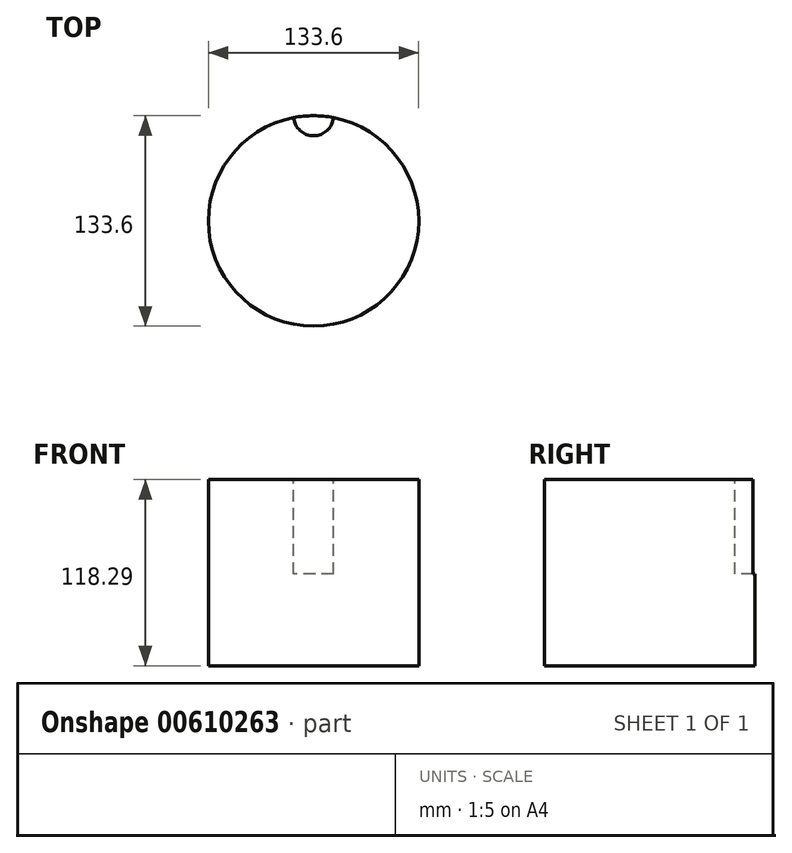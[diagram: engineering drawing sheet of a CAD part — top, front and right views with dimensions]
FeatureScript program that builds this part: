
annotation { "Feature Type Name" : "Feature", "Feature Type Description" : "" }
export const myFeature = defineFeature(function(context is Context, id is Id, definition is map)
    precondition{}
    {
        {
            var Q0;
            Q0=qCreatedBy(makeId("Top.planeOp"),FACE);
            var sketch = newSketch(context, id + "F0", { "sketchPlane" : qUnion([Q0])});
            skCircle(sketch, "E0", {"center": v(0, 0) * mm, "radius": 66.8 * mm});
            skSolve(sketch);
        }
        {
            var Q0;
            Q0 = qSketchRegion(id + "F0", true);
            extrude(context, id + "F1", {"entities" : qUnion([Q0]), "depth" : 118.3 * mm, "offsetDistance" : 25 * mm});
        }
        {
            var Q0;
            Q0=makeQuery(id+"F1.opExtrude","CAP_FACE",FACE,{"disambiguationData":[OSD([sQuery(id+"F0.wireOp",EDGE,"E0")])],"isStart":false});
            var sketch = newSketch(context, id + "F2", { "sketchPlane" : qUnion([Q0])});
            skSolve(sketch);
        }
        {
            var Q0;
            Q0=makeQuery(id+"F2.imprint","IMPRINT",FACE,{"disambiguationData":[TD([[makeQuery(id+"F2.imprint","IMPRINT",EDGE,{"derivedFrom":makeQuery(id+"F1.opExtrude","CAP_EDGE",EDGE,{"disambiguationData":[OSD([sQuery(id+"F0.wireOp",EDGE,"E0")])],"isStart":false})}),1.0]])]});
            var sketch = newSketch(context, id + "F3", { "sketchPlane" : qUnion([Q0])});
            skCircle(sketch, "E1", {"center": v(0, 66.75) * mm, "radius": 12.68 * mm});
            skSolve(sketch);
        }
        {
            var Q0;
            {var subQ0=sQuery(id+"F3.wireOp",EDGE,"E1");var subQ1=makeQuery(id+"F2.imprint","IMPRINT",EDGE,{"derivedFrom":makeQuery(id+"F1.opExtrude","CAP_EDGE",EDGE,{"disambiguationData":[OSD([sQuery(id+"F0.wireOp",EDGE,"E0")])],"isStart":false})});var subQ2=makeQuery(id+"F3.imprint","INTERSECT",VERTEX,{"disambiguationData":[OD(0.0)],"derivedFrom":[subQ1,subQ0]});Q0=makeQuery(id+"F3.imprint","IMPRINT",FACE,{"disambiguationData":[TD([[makeQuery(id+"F3.imprint","IMPRINT",EDGE,{"disambiguationData":[TD([[subQ2,1.0]])],"derivedFrom":subQ0}),1.0]])]});}
            var Q1;
            {var subQ0=sQuery(id+"F3.wireOp",EDGE,"E1");var subQ1=makeQuery(id+"F2.imprint","IMPRINT",EDGE,{"derivedFrom":makeQuery(id+"F1.opExtrude","CAP_EDGE",EDGE,{"disambiguationData":[OSD([sQuery(id+"F0.wireOp",EDGE,"E0")])],"isStart":false})});var subQ2=makeQuery(id+"F3.imprint","INTERSECT",VERTEX,{"disambiguationData":[OD(0.0)],"derivedFrom":[subQ1,subQ0]});Q1=makeQuery(id+"F3.imprint","IMPRINT",FACE,{"disambiguationData":[TD([[makeQuery(id+"F3.imprint","IMPRINT",EDGE,{"disambiguationData":[TD([[subQ2,-1.0]])],"derivedFrom":subQ0}),1.0]])]});}
            var Q2;
            Q2=sQuery(id+"F3.wireOp",EDGE,"E1");
            extrude(context, id + "F4", {"entities" : qUnion([Q0, Q1]), "operationType" : NewBodyOperationType.REMOVE, "surfaceEntities" : qUnion([Q2]), "oppositeDirection" : true, "depth" : 60 * mm, "offsetDistance" : 25 * mm});
        }
    });
